# Revit family: Naughtone_Tbls_Dalby_1100x550mmRectangularCoffee
name_source: partatom
category: Furniture
revit_build: Autodesk Revit 2015 (Build: 20160512_1515(x64)
units: mm (PartAtom-declared; Revit-internal decimal feet)

## types (1)
- Naughtone_Tbls_Dalby_1100x550mmRectangularCoffee
    AdditionalMaterials = Additional material and finish options available. Please contact Naughtone direct for further information.
    Assembly Code = E2020200
    AssetType = Movable
    BIMObjectName = Naughtone_Tables_Dalby_110x550mmRectangularCoffee
    Category = Pr_40_50_21_14 : Coffee Tables
    Color = White
    Constituents = Wood Top; Solid Oak frame
    Cost = 0 $
    Description = Dalby Rectangular Coffee Table
    DurationUnit = year
    ExpectedLife = 15-20
    IfcExportAs = IfcFurnishingElementType
    IfcExportType = TABLE
    Keynote = Pr_40_50_21_14
    MainColor = White
    ManufacturerAddressUK = Knaresborough Tech Park, Manse Lane, Knaresborough, HG5 8LF
    ManufacturerName = Naughtone
    ManufacturerURL = www.naughtone.com/
    Material = MFMDF Top; Solid Oak Legs
    Model = DAL-1100x550-LO
    ModelNumber = DAL-1100x550-LO
    ModelReference = Dalby Rectangular Coffee Table
    NBSDescription = Tables
    NBSReference = 45-35-86/327
    Name = Tables_Dalby_1100x550mmRectangularCoffee_Naughtone
    NominalHeight = 350 mm  [stored 1.14829 ft]
    NominalLength = 550 mm
    NominalWidth = 1100 mm
    NumberOfChairs = 0
    ProductInformation = www.naughtone.com/portfolio-view/dalby
    Shape = Rectangular
    Size = 550mmx1100mmx350mm
    URL = www.naughtone.com/
    Uniclass2015Description = Coffee tables
    Uniclass2015Reference = Pr_40_50_21_14
    Uniclass2015Version = Products v1.3
    Version = 1
    WarrantyDescription = 5 year warranty
    WarrantyDurationLabor = 5
    WarrantyDurationParts = 5
    WarrantyDurationUnit = year
    WarrantyStartDate = 1900-12-31T23:59:59
    WorksurfaceArea = 0 m²

note: [stored X ft] marks values corroborated as IEEE doubles in the binary element streams (Revit-internal decimal feet)

## geometry (parser evidence)
native form markers: Sweep x3
no freeform markers — native parametric forms only
